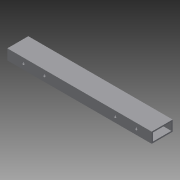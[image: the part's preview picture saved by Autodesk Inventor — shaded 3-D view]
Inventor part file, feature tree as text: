
AUTODESK INVENTOR PART (.ipt)
format: ipt  version: 2013 (Build 170138000, 138)  size: 104,448 bytes
history: native  units: in
note: dims shown in document units (in); Inventor stores cm internally (conversion verified against a paired STEP export)
features: extrude x3, sketch x3
ambient origin geometry x8: Origin, YZ Plane, XZ Plane, XY Plane, X Axis, Y Axis, Z Axis, Center Point
bodies: Solid1 (feature_tree)
feature tree (6):
  extrude  "Extrusion1"  Depth=2.0in
  extrude  "Extrusion2"  Depth=0.125in
  extrude  "Extrusion3"  Depth=1.75in
  sketch  "Sketch1"  dims[d0=13.75in d1=2.0in]
  sketch  "Sketch2"  dims[d2=1.0in d3=0.0in d4=0.125in]
  sketch  "Sketch3"  dims[d5=0.125in d6=1.75in d7=0.75in d8=20.0in d9=0.0in d10=1.5in d11=0.0in d12=2.0in d13=180.0deg d14=0.25in d15=0.25in d16=1.5in d17=180.0deg d18=2.0in d19=180.0deg d20=0.25in d21=0.25in d22=2.0in d23=0.0in]
